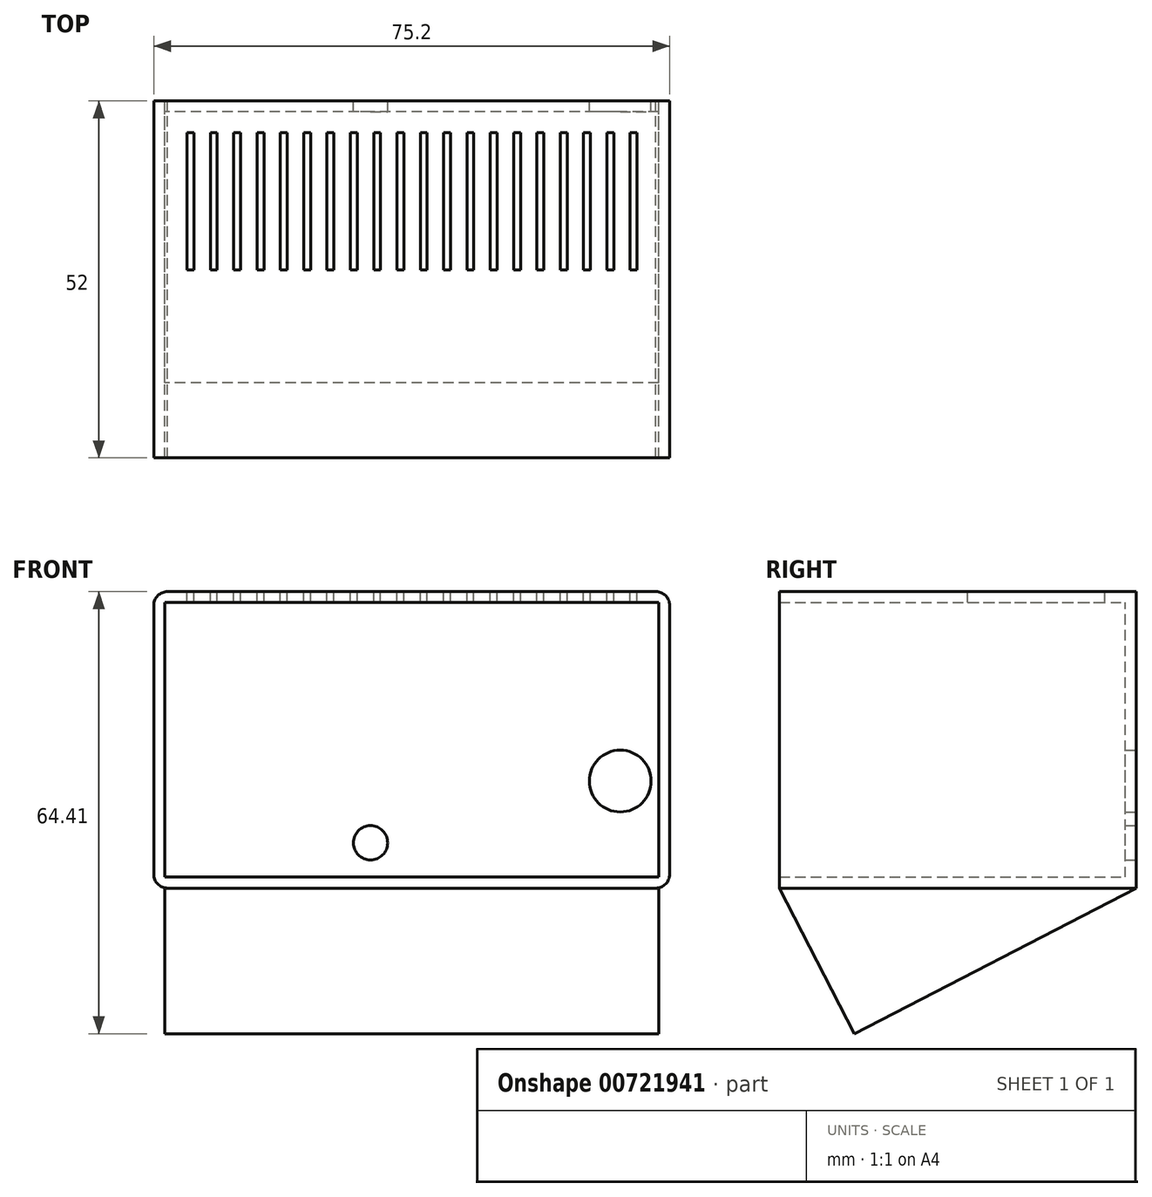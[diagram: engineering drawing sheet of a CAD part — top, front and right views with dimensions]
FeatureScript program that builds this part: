
annotation { "Feature Type Name" : "Feature", "Feature Type Description" : "" }
export const myFeature = defineFeature(function(context is Context, id is Id, definition is map)
    precondition{}
    {
        {
            var Q0;
            Q0=qCreatedBy(makeId("Front.planeOp"),FACE);
            var sketch = newSketch(context, id + "F0", { "sketchPlane" : qUnion([Q0])});
            skLineSegment(sketch, "E0.bottom", {"start": v(36, -20) * mm, "end": v(-36, -20) * mm});
            skLineSegment(sketch, "E0.top", {"start": v(36, 20) * mm, "end": v(-36, 20) * mm});
            skLineSegment(sketch, "E0.left", {"start": v(36, -20) * mm, "end": v(36, 20) * mm});
            skLineSegment(sketch, "E0.right", {"start": v(-36, -20) * mm, "end": v(-36, 20) * mm});
            skPoint(sketch, "E0.middle", {"position": v(0, 0) * mm});
            skLineSegment(sketch, "E1.0", {"start": v(-37.6, -21.6) * mm, "end": v(-37.6, 21.6) * mm});
            skLineSegment(sketch, "E1.1", {"start": v(37.6, -21.6) * mm, "end": v(-37.6, -21.6) * mm});
            skLineSegment(sketch, "E1.2", {"start": v(37.6, -21.6) * mm, "end": v(37.6, 21.6) * mm});
            skLineSegment(sketch, "E1.3", {"start": v(37.6, 21.6) * mm, "end": v(-37.6, 21.6) * mm});
            skPoint(sketch, "E2", {"position": v(30.4, -6) * mm});
            skPoint(sketch, "E3", {"position": v(-6, -15) * mm});
            skSolve(sketch);
        }
        {
            var Q0;
            Q0=makeQuery(id+"F0.imprint","IMPRINT",FACE,{"disambiguationData":[TD([[makeQuery(id+"F0.imprint","IMPRINT",EDGE,{"derivedFrom":sQuery(id+"F0.wireOp",EDGE,"E0.bottom")}),1.0]])]});
            extrude(context, id + "F1", {"entities" : qUnion([Q0]), "depth" : 52 * mm, "offsetDistance" : 25 * mm});
        }
        {
            var Q0;
            Q0=makeQuery(id+"F1.opExtrude","SWEPT_EDGE",EDGE,{"disambiguationData":[OSD([sQuery(id+"F0.wireOp",EDGE,"E1.2"),sQuery(id+"F0.wireOp",EDGE,"E1.3")])]});
            var Q1;
            Q1=makeQuery(id+"F1.opExtrude","SWEPT_EDGE",EDGE,{"disambiguationData":[OSD([sQuery(id+"F0.wireOp",EDGE,"E1.0"),sQuery(id+"F0.wireOp",EDGE,"E1.3")])]});
            var Q2;
            Q2=makeQuery(id+"F1.opExtrude","SWEPT_EDGE",EDGE,{"disambiguationData":[OSD([sQuery(id+"F0.wireOp",EDGE,"E1.0"),sQuery(id+"F0.wireOp",EDGE,"E1.1")])]});
            var Q3;
            Q3=makeQuery(id+"F1.opExtrude","SWEPT_EDGE",EDGE,{"disambiguationData":[OSD([sQuery(id+"F0.wireOp",EDGE,"E1.1"),sQuery(id+"F0.wireOp",EDGE,"E1.2")])]});
            fillet(context, id + "F2", {"entities" : qUnion([Q0, Q1, Q2, Q3]), "radius" : 2 * mm, "tangentPropagation" : true, "allowEdgeOverflow" : false});
        }
        {
            var Q0;
            Q0=makeQuery(id+"F0.imprint","IMPRINT",FACE,{"disambiguationData":[TD([[makeQuery(id+"F0.imprint","IMPRINT",EDGE,{"derivedFrom":sQuery(id+"F0.wireOp",EDGE,"E0.bottom")}),-1.0]])]});
            extrude(context, id + "F3", {"entities" : qUnion([Q0]), "operationType" : NewBodyOperationType.ADD, "depth" : 1.6 * mm, "offsetDistance" : 25 * mm});
        }
        {
            var Q0;
            Q0=qCreatedBy(makeId("Right.planeOp"),FACE);
            var sketch = newSketch(context, id + "F4", { "sketchPlane" : qUnion([Q0])});
            skPoint(sketch, "E4.0", {"position": v(-52, -21.6) * mm});
            skLineSegment(sketch, "E5", {"start": v(-52, -21.6) * mm, "end": v(-41.04, -42.8) * mm});
            skLineSegment(sketch, "E6", {"start": v(-41.04, -42.8) * mm, "end": v(0, -21.6) * mm});
            skLineSegment(sketch, "E7", {"start": v(-52, -21.6) * mm, "end": v(0, -21.6) * mm});
            skSolve(sketch);
        }
        {
            var Q0;
            Q0=makeQuery(id+"F4.imprint","IMPRINT",FACE,{"disambiguationData":[TD([[makeQuery(id+"F4.imprint","IMPRINT",EDGE,{"derivedFrom":sQuery(id+"F4.wireOp",EDGE,"E5")}),1.0]])]});
            extrude(context, id + "F5", {"entities" : qUnion([Q0]), "operationType" : NewBodyOperationType.ADD, "endBound" : BoundingType.SYMMETRIC, "depth" : 72 * mm, "offsetDistance" : 25 * mm});
        }
        {
            var Q0;
            Q0=sQuery(id+"F0.wireOp",VERTEX,"E2");
            var Q1;
            Q1=makeQuery(id+"F1.opExtrude","SWEPT_BODY",BODY,{"disambiguationData":[OSD([sQuery(id+"F0.wireOp",EDGE,"E0.bottom"),sQuery(id+"F0.wireOp",EDGE,"E0.top"),sQuery(id+"F0.wireOp",EDGE,"E0.left"),sQuery(id+"F0.wireOp",EDGE,"E0.right"),sQuery(id+"F0.wireOp",EDGE,"E1.0"),sQuery(id+"F0.wireOp",EDGE,"E1.1"),sQuery(id+"F0.wireOp",EDGE,"E1.2"),sQuery(id+"F0.wireOp",EDGE,"E1.3")])]});
            hole(context, id + "F6", {"style" : HoleStyle.SIMPLE, "endStyle" : HoleEndStyle.THROUGH, "oppositeDirection" : true, "holeDiameter" : 9 * mm, "majorDiameter" : 5 * mm, "isTappedThrough" : true, "tappedDepth" : 12 * mm, "tapClearance" : 3, "locations" : qUnion([Q0]), "scope" : qUnion([Q1])});
        }
        {
            var Q0;
            Q0=sQuery(id+"F0.wireOp",VERTEX,"E3");
            var Q1;
            Q1=makeQuery(id+"F1.opExtrude","SWEPT_BODY",BODY,{"disambiguationData":[OSD([sQuery(id+"F0.wireOp",EDGE,"E0.bottom"),sQuery(id+"F0.wireOp",EDGE,"E0.top"),sQuery(id+"F0.wireOp",EDGE,"E0.left"),sQuery(id+"F0.wireOp",EDGE,"E0.right"),sQuery(id+"F0.wireOp",EDGE,"E1.0"),sQuery(id+"F0.wireOp",EDGE,"E1.1"),sQuery(id+"F0.wireOp",EDGE,"E1.2"),sQuery(id+"F0.wireOp",EDGE,"E1.3")])]});
            hole(context, id + "F7", {"style" : HoleStyle.SIMPLE, "endStyle" : HoleEndStyle.THROUGH, "oppositeDirection" : true, "holeDiameter" : 5 * mm, "majorDiameter" : 5 * mm, "isTappedThrough" : true, "tappedDepth" : 12 * mm, "tapClearance" : 3, "locations" : qUnion([Q0]), "scope" : qUnion([Q1])});
        }
        {
            var Q0;
            Q0=makeQuery(id+"F1.opExtrude","SWEPT_FACE",FACE,{"disambiguationData":[OSD([sQuery(id+"F0.wireOp",EDGE,"E1.3")])]});
            var sketch = newSketch(context, id + "F8", { "sketchPlane" : qUnion([Q0])});
            skLineSegment(sketch, "E8.bottom", {"start": v(-32.74, -4.6) * mm, "end": v(-31.74, -4.6) * mm});
            skLineSegment(sketch, "E8.top", {"start": v(-32.74, -24.6) * mm, "end": v(-31.74, -24.6) * mm});
            skLineSegment(sketch, "E8.left", {"start": v(-32.74, -4.6) * mm, "end": v(-32.74, -24.6) * mm});
            skLineSegment(sketch, "E8.right", {"start": v(-31.74, -4.6) * mm, "end": v(-31.74, -24.6) * mm});
            skLineSegment(sketch, "E9.1.0.0", {"start": v(-29.34, -4.6) * mm, "end": v(-28.34, -4.6) * mm});
            skLineSegment(sketch, "E9.1.0.1", {"start": v(-29.34, -4.6) * mm, "end": v(-29.34, -24.6) * mm});
            skLineSegment(sketch, "E9.1.0.2", {"start": v(-28.34, -4.6) * mm, "end": v(-28.34, -24.6) * mm});
            skLineSegment(sketch, "E9.1.0.3", {"start": v(-29.34, -24.6) * mm, "end": v(-28.34, -24.6) * mm});
            skLineSegment(sketch, "E9.2.0.0", {"start": v(-25.94, -4.6) * mm, "end": v(-24.94, -4.6) * mm});
            skLineSegment(sketch, "E9.2.0.1", {"start": v(-25.94, -4.6) * mm, "end": v(-25.94, -24.6) * mm});
            skLineSegment(sketch, "E9.2.0.2", {"start": v(-24.94, -4.6) * mm, "end": v(-24.94, -24.6) * mm});
            skLineSegment(sketch, "E9.2.0.3", {"start": v(-25.94, -24.6) * mm, "end": v(-24.94, -24.6) * mm});
            skLineSegment(sketch, "E9.3.0.0", {"start": v(-22.54, -4.6) * mm, "end": v(-21.54, -4.6) * mm});
            skLineSegment(sketch, "E9.3.0.1", {"start": v(-22.54, -4.6) * mm, "end": v(-22.54, -24.6) * mm});
            skLineSegment(sketch, "E9.3.0.2", {"start": v(-21.54, -4.6) * mm, "end": v(-21.54, -24.6) * mm});
            skLineSegment(sketch, "E9.3.0.3", {"start": v(-22.54, -24.6) * mm, "end": v(-21.54, -24.6) * mm});
            skLineSegment(sketch, "E9.4.0.0", {"start": v(-19.14, -4.6) * mm, "end": v(-18.14, -4.6) * mm});
            skLineSegment(sketch, "E9.4.0.1", {"start": v(-19.14, -4.6) * mm, "end": v(-19.14, -24.6) * mm});
            skLineSegment(sketch, "E9.4.0.2", {"start": v(-18.14, -4.6) * mm, "end": v(-18.14, -24.6) * mm});
            skLineSegment(sketch, "E9.4.0.3", {"start": v(-19.14, -24.6) * mm, "end": v(-18.14, -24.6) * mm});
            skLineSegment(sketch, "E9.5.0.0", {"start": v(-15.74, -4.6) * mm, "end": v(-14.74, -4.6) * mm});
            skLineSegment(sketch, "E9.5.0.1", {"start": v(-15.74, -4.6) * mm, "end": v(-15.74, -24.6) * mm});
            skLineSegment(sketch, "E9.5.0.2", {"start": v(-14.74, -4.6) * mm, "end": v(-14.74, -24.6) * mm});
            skLineSegment(sketch, "E9.5.0.3", {"start": v(-15.74, -24.6) * mm, "end": v(-14.74, -24.6) * mm});
            skLineSegment(sketch, "E9.6.0.0", {"start": v(-12.34, -4.6) * mm, "end": v(-11.34, -4.6) * mm});
            skLineSegment(sketch, "E9.6.0.1", {"start": v(-12.34, -4.6) * mm, "end": v(-12.34, -24.6) * mm});
            skLineSegment(sketch, "E9.6.0.2", {"start": v(-11.34, -4.6) * mm, "end": v(-11.34, -24.6) * mm});
            skLineSegment(sketch, "E9.6.0.3", {"start": v(-12.34, -24.6) * mm, "end": v(-11.34, -24.6) * mm});
            skLineSegment(sketch, "E9.7.0.0", {"start": v(-8.94, -4.6) * mm, "end": v(-7.94, -4.6) * mm});
            skLineSegment(sketch, "E9.7.0.1", {"start": v(-8.94, -4.6) * mm, "end": v(-8.94, -24.6) * mm});
            skLineSegment(sketch, "E9.7.0.2", {"start": v(-7.94, -4.6) * mm, "end": v(-7.94, -24.6) * mm});
            skLineSegment(sketch, "E9.7.0.3", {"start": v(-8.94, -24.6) * mm, "end": v(-7.94, -24.6) * mm});
            skLineSegment(sketch, "E9.8.0.0", {"start": v(-5.54, -4.6) * mm, "end": v(-4.54, -4.6) * mm});
            skLineSegment(sketch, "E9.8.0.1", {"start": v(-5.54, -4.6) * mm, "end": v(-5.54, -24.6) * mm});
            skLineSegment(sketch, "E9.8.0.2", {"start": v(-4.54, -4.6) * mm, "end": v(-4.54, -24.6) * mm});
            skLineSegment(sketch, "E9.8.0.3", {"start": v(-5.54, -24.6) * mm, "end": v(-4.54, -24.6) * mm});
            skLineSegment(sketch, "E9.9.0.0", {"start": v(-2.14, -4.6) * mm, "end": v(-1.14, -4.6) * mm});
            skLineSegment(sketch, "E9.9.0.1", {"start": v(-2.14, -4.6) * mm, "end": v(-2.14, -24.6) * mm});
            skLineSegment(sketch, "E9.9.0.2", {"start": v(-1.14, -4.6) * mm, "end": v(-1.14, -24.6) * mm});
            skLineSegment(sketch, "E9.9.0.3", {"start": v(-2.14, -24.6) * mm, "end": v(-1.14, -24.6) * mm});
            skLineSegment(sketch, "E9.10.0.0", {"start": v(1.26, -4.6) * mm, "end": v(2.26, -4.6) * mm});
            skLineSegment(sketch, "E9.10.0.1", {"start": v(1.26, -4.6) * mm, "end": v(1.26, -24.6) * mm});
            skLineSegment(sketch, "E9.10.0.2", {"start": v(2.26, -4.6) * mm, "end": v(2.26, -24.6) * mm});
            skLineSegment(sketch, "E9.10.0.3", {"start": v(1.26, -24.6) * mm, "end": v(2.26, -24.6) * mm});
            skLineSegment(sketch, "E9.11.0.0", {"start": v(4.66, -4.6) * mm, "end": v(5.66, -4.6) * mm});
            skLineSegment(sketch, "E9.11.0.1", {"start": v(4.66, -4.6) * mm, "end": v(4.66, -24.6) * mm});
            skLineSegment(sketch, "E9.11.0.2", {"start": v(5.66, -4.6) * mm, "end": v(5.66, -24.6) * mm});
            skLineSegment(sketch, "E9.11.0.3", {"start": v(4.66, -24.6) * mm, "end": v(5.66, -24.6) * mm});
            skLineSegment(sketch, "E9.12.0.0", {"start": v(8.06, -4.6) * mm, "end": v(9.06, -4.6) * mm});
            skLineSegment(sketch, "E9.12.0.1", {"start": v(8.06, -4.6) * mm, "end": v(8.06, -24.6) * mm});
            skLineSegment(sketch, "E9.12.0.2", {"start": v(9.06, -4.6) * mm, "end": v(9.06, -24.6) * mm});
            skLineSegment(sketch, "E9.12.0.3", {"start": v(8.06, -24.6) * mm, "end": v(9.06, -24.6) * mm});
            skLineSegment(sketch, "E9.13.0.0", {"start": v(11.46, -4.6) * mm, "end": v(12.46, -4.6) * mm});
            skLineSegment(sketch, "E9.13.0.1", {"start": v(11.46, -4.6) * mm, "end": v(11.46, -24.6) * mm});
            skLineSegment(sketch, "E9.13.0.2", {"start": v(12.46, -4.6) * mm, "end": v(12.46, -24.6) * mm});
            skLineSegment(sketch, "E9.13.0.3", {"start": v(11.46, -24.6) * mm, "end": v(12.46, -24.6) * mm});
            skLineSegment(sketch, "E9.14.0.0", {"start": v(14.86, -4.6) * mm, "end": v(15.86, -4.6) * mm});
            skLineSegment(sketch, "E9.14.0.1", {"start": v(14.86, -4.6) * mm, "end": v(14.86, -24.6) * mm});
            skLineSegment(sketch, "E9.14.0.2", {"start": v(15.86, -4.6) * mm, "end": v(15.86, -24.6) * mm});
            skLineSegment(sketch, "E9.14.0.3", {"start": v(14.86, -24.6) * mm, "end": v(15.86, -24.6) * mm});
            skLineSegment(sketch, "E9.15.0.0", {"start": v(18.26, -4.6) * mm, "end": v(19.26, -4.6) * mm});
            skLineSegment(sketch, "E9.15.0.1", {"start": v(18.26, -4.6) * mm, "end": v(18.26, -24.6) * mm});
            skLineSegment(sketch, "E9.15.0.2", {"start": v(19.26, -4.6) * mm, "end": v(19.26, -24.6) * mm});
            skLineSegment(sketch, "E9.15.0.3", {"start": v(18.26, -24.6) * mm, "end": v(19.26, -24.6) * mm});
            skLineSegment(sketch, "E9.16.0.0", {"start": v(21.66, -4.6) * mm, "end": v(22.66, -4.6) * mm});
            skLineSegment(sketch, "E9.16.0.1", {"start": v(21.66, -4.6) * mm, "end": v(21.66, -24.6) * mm});
            skLineSegment(sketch, "E9.16.0.2", {"start": v(22.66, -4.6) * mm, "end": v(22.66, -24.6) * mm});
            skLineSegment(sketch, "E9.16.0.3", {"start": v(21.66, -24.6) * mm, "end": v(22.66, -24.6) * mm});
            skLineSegment(sketch, "E9.17.0.0", {"start": v(25.06, -4.6) * mm, "end": v(26.06, -4.6) * mm});
            skLineSegment(sketch, "E9.17.0.1", {"start": v(25.06, -4.6) * mm, "end": v(25.06, -24.6) * mm});
            skLineSegment(sketch, "E9.17.0.2", {"start": v(26.06, -4.6) * mm, "end": v(26.06, -24.6) * mm});
            skLineSegment(sketch, "E9.17.0.3", {"start": v(25.06, -24.6) * mm, "end": v(26.06, -24.6) * mm});
            skLineSegment(sketch, "E9.18.0.0", {"start": v(28.46, -4.6) * mm, "end": v(29.46, -4.6) * mm});
            skLineSegment(sketch, "E9.18.0.1", {"start": v(28.46, -4.6) * mm, "end": v(28.46, -24.6) * mm});
            skLineSegment(sketch, "E9.18.0.2", {"start": v(29.46, -4.6) * mm, "end": v(29.46, -24.6) * mm});
            skLineSegment(sketch, "E9.18.0.3", {"start": v(28.46, -24.6) * mm, "end": v(29.46, -24.6) * mm});
            skLineSegment(sketch, "E9.19.0.0", {"start": v(31.86, -4.6) * mm, "end": v(32.86, -4.6) * mm});
            skLineSegment(sketch, "E9.19.0.1", {"start": v(31.86, -4.6) * mm, "end": v(31.86, -24.6) * mm});
            skLineSegment(sketch, "E9.19.0.2", {"start": v(32.86, -4.6) * mm, "end": v(32.86, -24.6) * mm});
            skLineSegment(sketch, "E9.19.0.3", {"start": v(31.86, -24.6) * mm, "end": v(32.86, -24.6) * mm});
            skLineSegment(sketch, "E9.direction1", {"start": v(-32.74, -4.6) * mm, "end": v(-29.34, -4.6) * mm, "construction": true});
            skSolve(sketch);
        }
        {
            var Q0;
            Q0=makeQuery(id+"F8.imprint","IMPRINT",FACE,{"disambiguationData":[TD([[makeQuery(id+"F8.imprint","IMPRINT",EDGE,{"derivedFrom":sQuery(id+"F8.wireOp",EDGE,"E8.bottom")}),-1.0]])]});
            var Q1;
            Q1=makeQuery(id+"F8.imprint","IMPRINT",FACE,{"disambiguationData":[TD([[makeQuery(id+"F8.imprint","IMPRINT",EDGE,{"derivedFrom":sQuery(id+"F8.wireOp",EDGE,"E9.1.0.0")}),-1.0]])]});
            var Q2;
            Q2=makeQuery(id+"F8.imprint","IMPRINT",FACE,{"disambiguationData":[TD([[makeQuery(id+"F8.imprint","IMPRINT",EDGE,{"derivedFrom":sQuery(id+"F8.wireOp",EDGE,"E9.2.0.0")}),-1.0]])]});
            var Q3;
            Q3=makeQuery(id+"F8.imprint","IMPRINT",FACE,{"disambiguationData":[TD([[makeQuery(id+"F8.imprint","IMPRINT",EDGE,{"derivedFrom":sQuery(id+"F8.wireOp",EDGE,"E9.3.0.0")}),-1.0]])]});
            var Q4;
            Q4=makeQuery(id+"F8.imprint","IMPRINT",FACE,{"disambiguationData":[TD([[makeQuery(id+"F8.imprint","IMPRINT",EDGE,{"derivedFrom":sQuery(id+"F8.wireOp",EDGE,"E9.4.0.0")}),-1.0]])]});
            var Q5;
            Q5=makeQuery(id+"F8.imprint","IMPRINT",FACE,{"disambiguationData":[TD([[makeQuery(id+"F8.imprint","IMPRINT",EDGE,{"derivedFrom":sQuery(id+"F8.wireOp",EDGE,"E9.5.0.0")}),-1.0]])]});
            var Q6;
            Q6=makeQuery(id+"F8.imprint","IMPRINT",FACE,{"disambiguationData":[TD([[makeQuery(id+"F8.imprint","IMPRINT",EDGE,{"derivedFrom":sQuery(id+"F8.wireOp",EDGE,"E9.6.0.0")}),-1.0]])]});
            var Q7;
            Q7=makeQuery(id+"F8.imprint","IMPRINT",FACE,{"disambiguationData":[TD([[makeQuery(id+"F8.imprint","IMPRINT",EDGE,{"derivedFrom":sQuery(id+"F8.wireOp",EDGE,"E9.7.0.0")}),-1.0]])]});
            var Q8;
            Q8=makeQuery(id+"F8.imprint","IMPRINT",FACE,{"disambiguationData":[TD([[makeQuery(id+"F8.imprint","IMPRINT",EDGE,{"derivedFrom":sQuery(id+"F8.wireOp",EDGE,"E9.8.0.0")}),-1.0]])]});
            var Q9;
            Q9=makeQuery(id+"F8.imprint","IMPRINT",FACE,{"disambiguationData":[TD([[makeQuery(id+"F8.imprint","IMPRINT",EDGE,{"derivedFrom":sQuery(id+"F8.wireOp",EDGE,"E9.10.0.0")}),-1.0]])]});
            var Q10;
            Q10=makeQuery(id+"F8.imprint","IMPRINT",FACE,{"disambiguationData":[TD([[makeQuery(id+"F8.imprint","IMPRINT",EDGE,{"derivedFrom":sQuery(id+"F8.wireOp",EDGE,"E9.11.0.0")}),-1.0]])]});
            var Q11;
            Q11=makeQuery(id+"F8.imprint","IMPRINT",FACE,{"disambiguationData":[TD([[makeQuery(id+"F8.imprint","IMPRINT",EDGE,{"derivedFrom":sQuery(id+"F8.wireOp",EDGE,"E9.9.0.0")}),-1.0]])]});
            var Q12;
            Q12=makeQuery(id+"F8.imprint","IMPRINT",FACE,{"disambiguationData":[TD([[makeQuery(id+"F8.imprint","IMPRINT",EDGE,{"derivedFrom":sQuery(id+"F8.wireOp",EDGE,"E9.12.0.0")}),-1.0]])]});
            var Q13;
            Q13=makeQuery(id+"F8.imprint","IMPRINT",FACE,{"disambiguationData":[TD([[makeQuery(id+"F8.imprint","IMPRINT",EDGE,{"derivedFrom":sQuery(id+"F8.wireOp",EDGE,"E9.13.0.0")}),-1.0]])]});
            var Q14;
            Q14=makeQuery(id+"F8.imprint","IMPRINT",FACE,{"disambiguationData":[TD([[makeQuery(id+"F8.imprint","IMPRINT",EDGE,{"derivedFrom":sQuery(id+"F8.wireOp",EDGE,"E9.14.0.0")}),-1.0]])]});
            var Q15;
            Q15=makeQuery(id+"F8.imprint","IMPRINT",FACE,{"disambiguationData":[TD([[makeQuery(id+"F8.imprint","IMPRINT",EDGE,{"derivedFrom":sQuery(id+"F8.wireOp",EDGE,"E9.15.0.0")}),-1.0]])]});
            var Q16;
            Q16=makeQuery(id+"F8.imprint","IMPRINT",FACE,{"disambiguationData":[TD([[makeQuery(id+"F8.imprint","IMPRINT",EDGE,{"derivedFrom":sQuery(id+"F8.wireOp",EDGE,"E9.16.0.0")}),-1.0]])]});
            var Q17;
            Q17=makeQuery(id+"F8.imprint","IMPRINT",FACE,{"disambiguationData":[TD([[makeQuery(id+"F8.imprint","IMPRINT",EDGE,{"derivedFrom":sQuery(id+"F8.wireOp",EDGE,"E9.17.0.0")}),-1.0]])]});
            var Q18;
            Q18=makeQuery(id+"F8.imprint","IMPRINT",FACE,{"disambiguationData":[TD([[makeQuery(id+"F8.imprint","IMPRINT",EDGE,{"derivedFrom":sQuery(id+"F8.wireOp",EDGE,"E9.18.0.0")}),-1.0]])]});
            var Q19;
            Q19=makeQuery(id+"F8.imprint","IMPRINT",FACE,{"disambiguationData":[TD([[makeQuery(id+"F8.imprint","IMPRINT",EDGE,{"derivedFrom":sQuery(id+"F8.wireOp",EDGE,"E9.19.0.0")}),-1.0]])]});
            extrude(context, id + "F9", {"entities" : qUnion([Q0, Q1, Q2, Q3, Q4, Q5, Q6, Q7, Q8, Q9, Q10, Q11, Q12, Q13, Q14, Q15, Q16, Q17, Q18, Q19]), "operationType" : NewBodyOperationType.REMOVE, "oppositeDirection" : true, "depth" : 25 * mm, "offsetDistance" : 25 * mm});
        }
    });
